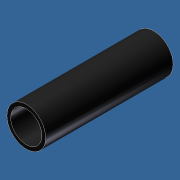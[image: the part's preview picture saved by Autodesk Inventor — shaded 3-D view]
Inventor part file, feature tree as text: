
AUTODESK INVENTOR PART (.ipt)
format: ipt  version: unknown  size: 164,352 bytes
history: native  units: in
note: dims shown in document units (in); Inventor stores cm internally (conversion verified against a paired STEP export)
features: extrude x1, sketch x1
ambient origin geometry x8: Origin, YZ Plane, XZ Plane, XY Plane, X Axis, Y Axis, Z Axis, Center Point
bodies: Solid1 (feature_tree)
feature tree (2):
  extrude  "Extrusion1"  Depth=0.201in
  sketch  "Sketch1"  dims[d0=0.25in d1=0.201in d2=0.8213in d3=0.0in]
